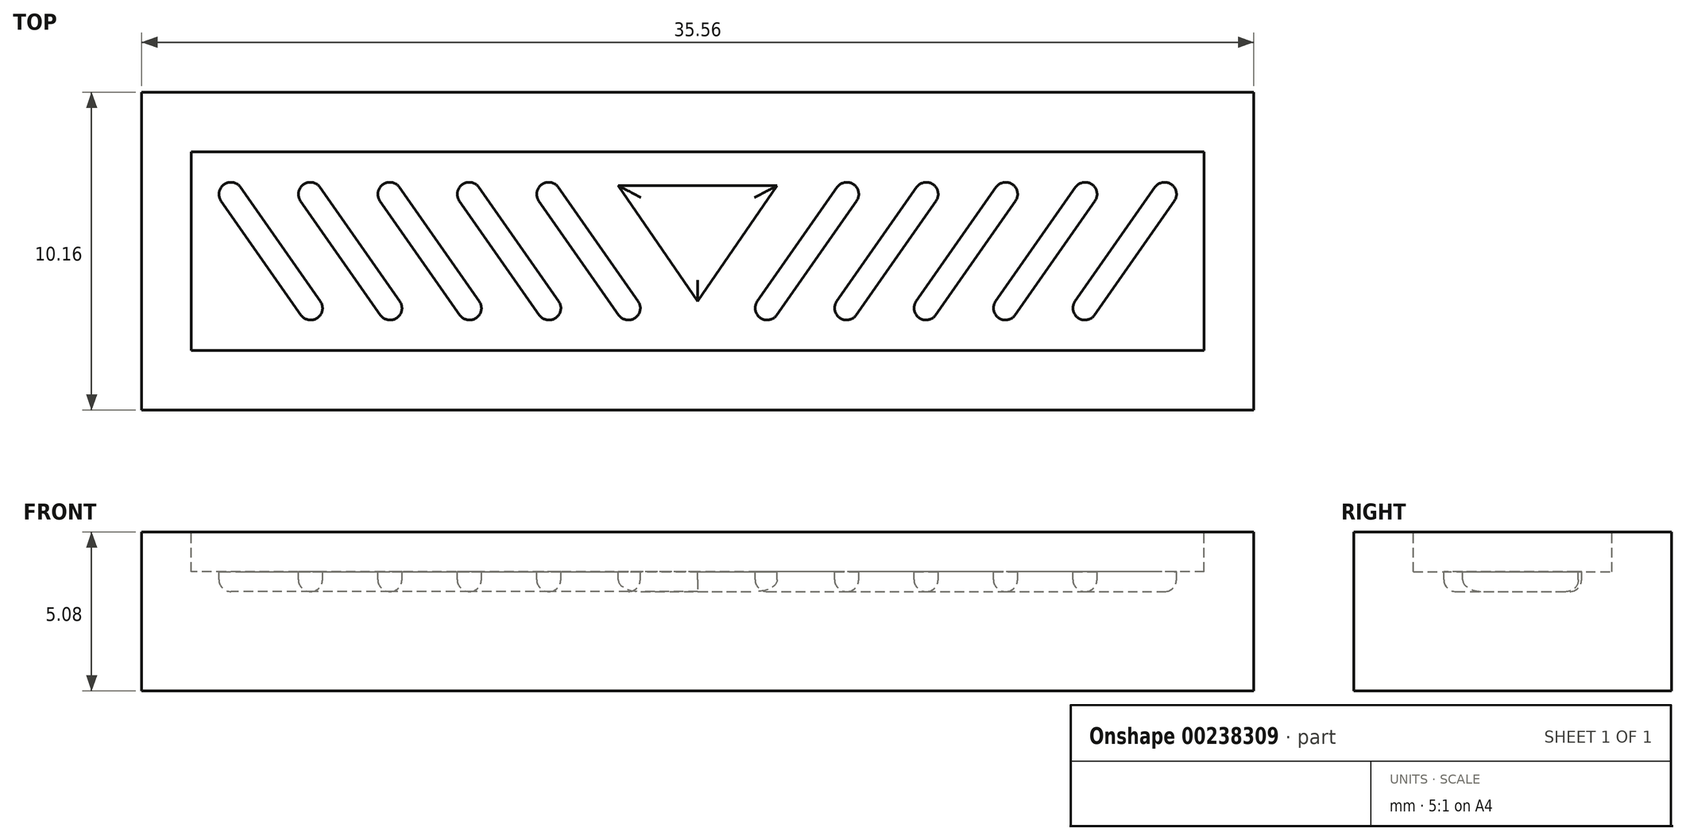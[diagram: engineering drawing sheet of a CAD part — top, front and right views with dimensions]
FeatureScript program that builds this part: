
annotation { "Feature Type Name" : "Feature", "Feature Type Description" : "" }
export const myFeature = defineFeature(function(context is Context, id is Id, definition is map)
    precondition{}
    {
        {
            var Q0;
            Q0=qCreatedBy(makeId("Top.planeOp"),FACE);
            var sketch = newSketch(context, id + "F0", { "sketchPlane" : qUnion([Q0])});
            skLineSegment(sketch, "E0.bottom", {"start": v(17.78, -5.08) * mm, "end": v(-17.78, -5.08) * mm});
            skLineSegment(sketch, "E0.top", {"start": v(17.78, 5.08) * mm, "end": v(-17.78, 5.08) * mm});
            skLineSegment(sketch, "E0.left", {"start": v(17.78, -5.08) * mm, "end": v(17.78, 5.08) * mm});
            skLineSegment(sketch, "E0.right", {"start": v(-17.78, -5.08) * mm, "end": v(-17.78, 5.08) * mm});
            skPoint(sketch, "E0.middle", {"position": v(0, 0) * mm});
            skSolve(sketch);
        }
        {
            var Q0;
            Q0=makeQuery(id+"F0.imprint","IMPRINT",FACE,{"disambiguationData":[TD([[makeQuery(id+"F0.imprint","IMPRINT",EDGE,{"derivedFrom":sQuery(id+"F0.wireOp",EDGE,"E0.bottom")}),-1.0]])]});
            extrude(context, id + "F1", {"entities" : qUnion([Q0]), "depth" : 5.08 * mm});
        }
        {
            var Q0;
            Q0=makeQuery(id+"F1.opExtrude","CAP_FACE",FACE,{"disambiguationData":[OSD([sQuery(id+"F0.wireOp",EDGE,"E0.bottom"),sQuery(id+"F0.wireOp",EDGE,"E0.top"),sQuery(id+"F0.wireOp",EDGE,"E0.left"),sQuery(id+"F0.wireOp",EDGE,"E0.right")])],"isStart":false});
            var sketch = newSketch(context, id + "F2", { "sketchPlane" : qUnion([Q0])});
            skLineSegment(sketch, "E1.bottom", {"start": v(16.2, -3.18) * mm, "end": v(-16.2, -3.18) * mm});
            skLineSegment(sketch, "E1.top", {"start": v(16.2, 3.18) * mm, "end": v(-16.2, 3.18) * mm});
            skLineSegment(sketch, "E1.left", {"start": v(16.2, -3.18) * mm, "end": v(16.2, 3.17) * mm});
            skLineSegment(sketch, "E1.right", {"start": v(-16.2, -3.18) * mm, "end": v(-16.2, 3.17) * mm});
            skPoint(sketch, "E1.middle", {"position": v(0, 0) * mm});
            skSolve(sketch);
        }
        {
            var Q0;
            Q0=qSketchRegion(id+"F2",true);
            extrude(context, id + "F3", {"entities" : qUnion([Q0]), "operationType" : NewBodyOperationType.REMOVE, "oppositeDirection" : true, "depth" : 1.27 * mm});
        }
        {
            var Q0;
            Q0=makeQuery(id+"F3.boolean.opBoolean","COPY",FACE,{"derivedFrom":makeQuery(id+"F3.opExtrude","CAP_FACE",FACE,{"disambiguationData":[OSD([sQuery(id+"F2.wireOp",EDGE,"E1.bottom"),sQuery(id+"F2.wireOp",EDGE,"E1.top"),sQuery(id+"F2.wireOp",EDGE,"E1.left"),sQuery(id+"F2.wireOp",EDGE,"E1.right")])],"isStart":false})});
            var sketch = newSketch(context, id + "F4", { "sketchPlane" : qUnion([Q0])});
            skLineSegment(sketch, "E2", {"start": v(-14.93, 1.82) * mm, "end": v(-12.38, -1.82) * mm});
            skArc(sketch, "E3.0.startCap", {"start": v(-15.24, 1.6) * mm, "mid": v(-15.15, 2.13) * mm, "end": v(-14.62, 2.04) * mm});
            skArc(sketch, "E3.0.endCap", {"start": v(-12.07, -1.6) * mm, "mid": v(-12.16, -2.13) * mm, "end": v(-12.69, -2.04) * mm});
            skLineSegment(sketch, "E3.0.left", {"start": v(-14.62, 2.04) * mm, "end": v(-12.07, -1.6) * mm});
            skLineSegment(sketch, "E3.0.right", {"start": v(-15.24, 1.6) * mm, "end": v(-12.69, -2.04) * mm});
            skPoint(sketch, "E4", {"position": v(-13.65, 0) * mm});
            skLineSegment(sketch, "E5.1.0.0", {"start": v(-12.08, 2.04) * mm, "end": v(-9.53, -1.6) * mm});
            skArc(sketch, "E5.1.0.1", {"start": v(-12.7, 1.6) * mm, "mid": v(-12.6, 2.13) * mm, "end": v(-12.08, 2.04) * mm});
            skLineSegment(sketch, "E5.1.0.2", {"start": v(-12.7, 1.6) * mm, "end": v(-10.15, -2.04) * mm});
            skArc(sketch, "E5.1.0.3", {"start": v(-9.53, -1.6) * mm, "mid": v(-9.62, -2.13) * mm, "end": v(-10.15, -2.04) * mm});
            skLineSegment(sketch, "E5.2.0.0", {"start": v(-9.54, 2.04) * mm, "end": v(-6.99, -1.6) * mm});
            skArc(sketch, "E5.2.0.1", {"start": v(-10.16, 1.6) * mm, "mid": v(-10.07, 2.13) * mm, "end": v(-9.54, 2.04) * mm});
            skLineSegment(sketch, "E5.2.0.2", {"start": v(-10.16, 1.6) * mm, "end": v(-7.6, -2.04) * mm});
            skArc(sketch, "E5.2.0.3", {"start": v(-6.99, -1.6) * mm, "mid": v(-7.08, -2.13) * mm, "end": v(-7.6, -2.04) * mm});
            skLineSegment(sketch, "E5.3.0.0", {"start": v(-7, 2.04) * mm, "end": v(-4.45, -1.6) * mm});
            skArc(sketch, "E5.3.0.1", {"start": v(-7.62, 1.6) * mm, "mid": v(-7.53, 2.13) * mm, "end": v(-7, 2.04) * mm});
            skLineSegment(sketch, "E5.3.0.2", {"start": v(-7.62, 1.6) * mm, "end": v(-5.07, -2.04) * mm});
            skArc(sketch, "E5.3.0.3", {"start": v(-4.45, -1.6) * mm, "mid": v(-4.54, -2.13) * mm, "end": v(-5.07, -2.04) * mm});
            skLineSegment(sketch, "E5.4.0.0", {"start": v(-4.46, 2.04) * mm, "end": v(-1.9, -1.6) * mm});
            skArc(sketch, "E5.4.0.1", {"start": v(-5.08, 1.6) * mm, "mid": v(-4.99, 2.13) * mm, "end": v(-4.46, 2.04) * mm});
            skLineSegment(sketch, "E5.4.0.2", {"start": v(-5.08, 1.6) * mm, "end": v(-2.53, -2.04) * mm});
            skArc(sketch, "E5.4.0.3", {"start": v(-1.9, -1.6) * mm, "mid": v(-2, -2.13) * mm, "end": v(-2.53, -2.04) * mm});
            skLineSegment(sketch, "E5.direction1", {"start": v(-12.69, -2.04) * mm, "end": v(-10.15, -2.04) * mm, "construction": true});
            skLineSegment(sketch, "E6", {"start": v(0, 3.17) * mm, "end": v(0, -3.18) * mm, "construction": true});
            skLineSegment(sketch, "E7.MirrorCS", {"start": v(15.24, 1.6) * mm, "end": v(12.69, -2.04) * mm});
            skLineSegment(sketch, "E8.MirrorCS", {"start": v(14.62, 2.04) * mm, "end": v(12.07, -1.6) * mm});
            skArc(sketch, "E9.MirrorCS", {"start": v(15.24, 1.6) * mm, "mid": v(15.15, 2.13) * mm, "end": v(14.62, 2.04) * mm});
            skArc(sketch, "E10.MirrorCS", {"start": v(12.07, -1.6) * mm, "mid": v(12.16, -2.13) * mm, "end": v(12.69, -2.04) * mm});
            skLineSegment(sketch, "E11.MirrorCS", {"start": v(12.7, 1.6) * mm, "end": v(10.15, -2.04) * mm});
            skArc(sketch, "E12.MirrorCS", {"start": v(12.7, 1.6) * mm, "mid": v(12.6, 2.13) * mm, "end": v(12.08, 2.04) * mm});
            skLineSegment(sketch, "E13.MirrorCS", {"start": v(12.08, 2.04) * mm, "end": v(9.53, -1.6) * mm});
            skArc(sketch, "E14.MirrorCS", {"start": v(9.53, -1.6) * mm, "mid": v(9.62, -2.13) * mm, "end": v(10.15, -2.04) * mm});
            skArc(sketch, "E15.MirrorCS", {"start": v(6.99, -1.6) * mm, "mid": v(7.08, -2.13) * mm, "end": v(7.6, -2.04) * mm});
            skLineSegment(sketch, "E16.MirrorCS", {"start": v(10.16, 1.6) * mm, "end": v(7.6, -2.04) * mm});
            skLineSegment(sketch, "E17.MirrorCS", {"start": v(9.54, 2.04) * mm, "end": v(6.99, -1.6) * mm});
            skArc(sketch, "E18.MirrorCS", {"start": v(10.16, 1.6) * mm, "mid": v(10.07, 2.13) * mm, "end": v(9.54, 2.04) * mm});
            skArc(sketch, "E19.MirrorCS", {"start": v(7.62, 1.6) * mm, "mid": v(7.53, 2.13) * mm, "end": v(7, 2.04) * mm});
            skArc(sketch, "E20.MirrorCS", {"start": v(5.08, 1.6) * mm, "mid": v(4.99, 2.13) * mm, "end": v(4.46, 2.04) * mm});
            skLineSegment(sketch, "E21.MirrorCS", {"start": v(7.62, 1.6) * mm, "end": v(5.07, -2.04) * mm});
            skLineSegment(sketch, "E22.MirrorCS", {"start": v(7, 2.04) * mm, "end": v(4.45, -1.6) * mm});
            skLineSegment(sketch, "E23.MirrorCS", {"start": v(5.08, 1.6) * mm, "end": v(2.53, -2.04) * mm});
            skLineSegment(sketch, "E24.MirrorCS", {"start": v(4.46, 2.04) * mm, "end": v(1.9, -1.6) * mm});
            skArc(sketch, "E25.MirrorCS", {"start": v(4.45, -1.6) * mm, "mid": v(4.54, -2.13) * mm, "end": v(5.07, -2.04) * mm});
            skArc(sketch, "E26.MirrorCS", {"start": v(1.9, -1.6) * mm, "mid": v(2, -2.13) * mm, "end": v(2.53, -2.04) * mm});
            skLineSegment(sketch, "E27", {"start": v(0, -1.6) * mm, "end": v(-2.54, 2.1) * mm});
            skLineSegment(sketch, "E28", {"start": v(-2.54, 2.1) * mm, "end": v(0, 2.1) * mm});
            skLineSegment(sketch, "E29", {"start": v(0, 2.1) * mm, "end": v(0, -1.6) * mm});
            skLineSegment(sketch, "E30.MirrorCS", {"start": v(2.54, 2.1) * mm, "end": v(0, 2.1) * mm});
            skLineSegment(sketch, "E31.MirrorCS", {"start": v(0, -1.6) * mm, "end": v(2.54, 2.1) * mm});
            skSolve(sketch);
        }
        {
            var Q0;
            Q0 = qSketchRegion(id + "F4", true);
            extrude(context, id + "F5", {"entities" : qUnion([Q0]), "operationType" : NewBodyOperationType.REMOVE, "oppositeDirection" : true, "depth" : 0.64 * mm});
        }
        {
            var Q0;
            Q0=makeQuery(id+"F5.boolean.opBoolean","COPY",EDGE,{"derivedFrom":makeQuery(id+"F5.opExtrude","CAP_EDGE",EDGE,{"disambiguationData":[OSD([sQuery(id+"F4.wireOp",EDGE,"E5.1.0.0")])],"isStart":false})});
            var Q1;
            Q1=makeQuery(id+"F5.boolean.opBoolean","COPY",EDGE,{"derivedFrom":makeQuery(id+"F5.opExtrude","CAP_EDGE",EDGE,{"disambiguationData":[OSD([sQuery(id+"F4.wireOp",EDGE,"E3.0.right")])],"isStart":false})});
            var Q2;
            Q2=makeQuery(id+"F5.boolean.opBoolean","COPY",EDGE,{"derivedFrom":makeQuery(id+"F5.opExtrude","CAP_EDGE",EDGE,{"disambiguationData":[OSD([sQuery(id+"F4.wireOp",EDGE,"E5.2.0.2")])],"isStart":false})});
            var Q3;
            Q3=makeQuery(id+"F5.boolean.opBoolean","COPY",EDGE,{"derivedFrom":makeQuery(id+"F5.opExtrude","CAP_EDGE",EDGE,{"disambiguationData":[OSD([sQuery(id+"F4.wireOp",EDGE,"E5.3.0.2")])],"isStart":false})});
            var Q4;
            Q4=makeQuery(id+"F5.boolean.opBoolean","COPY",EDGE,{"derivedFrom":makeQuery(id+"F5.opExtrude","CAP_EDGE",EDGE,{"disambiguationData":[OSD([sQuery(id+"F4.wireOp",EDGE,"E5.4.0.2")])],"isStart":false})});
            var Q5;
            Q5=makeQuery(id+"F5.boolean.opBoolean","COPY",EDGE,{"derivedFrom":makeQuery(id+"F5.opExtrude","CAP_EDGE",EDGE,{"disambiguationData":[OSD([sQuery(id+"F4.wireOp",EDGE,"E24.MirrorCS")])],"isStart":false})});
            var Q6;
            Q6=makeQuery(id+"F5.boolean.opBoolean","COPY",EDGE,{"derivedFrom":makeQuery(id+"F5.opExtrude","CAP_EDGE",EDGE,{"disambiguationData":[OSD([sQuery(id+"F4.wireOp",EDGE,"E22.MirrorCS")])],"isStart":false})});
            var Q7;
            Q7=makeQuery(id+"F5.boolean.opBoolean","COPY",EDGE,{"derivedFrom":makeQuery(id+"F5.opExtrude","CAP_EDGE",EDGE,{"disambiguationData":[OSD([sQuery(id+"F4.wireOp",EDGE,"E17.MirrorCS")])],"isStart":false})});
            var Q8;
            Q8=makeQuery(id+"F5.boolean.opBoolean","COPY",EDGE,{"derivedFrom":makeQuery(id+"F5.opExtrude","CAP_EDGE",EDGE,{"disambiguationData":[OSD([sQuery(id+"F4.wireOp",EDGE,"E13.MirrorCS")])],"isStart":false})});
            var Q9;
            Q9=makeQuery(id+"F5.boolean.opBoolean","COPY",EDGE,{"derivedFrom":makeQuery(id+"F5.opExtrude","CAP_EDGE",EDGE,{"disambiguationData":[OSD([sQuery(id+"F4.wireOp",EDGE,"E8.MirrorCS")])],"isStart":false})});
            var Q10;
            Q10=makeQuery(id+"F5.boolean.opBoolean","COPY",EDGE,{"derivedFrom":makeQuery(id+"F5.opExtrude","CAP_EDGE",EDGE,{"disambiguationData":[OSD([sQuery(id+"F4.wireOp",EDGE,"E28"),sQuery(id+"F4.wireOp",EDGE,"E30.MirrorCS")])],"isStart":false})});
            var Q11;
            Q11=makeQuery(id+"F5.boolean.opBoolean","COPY",EDGE,{"derivedFrom":makeQuery(id+"F5.opExtrude","CAP_EDGE",EDGE,{"disambiguationData":[OSD([sQuery(id+"F4.wireOp",EDGE,"E27")])],"isStart":false})});
            var Q12;
            Q12=makeQuery(id+"F5.boolean.opBoolean","COPY",EDGE,{"derivedFrom":makeQuery(id+"F5.opExtrude","CAP_EDGE",EDGE,{"disambiguationData":[OSD([sQuery(id+"F4.wireOp",EDGE,"E31.MirrorCS")])],"isStart":false})});
            fillet(context, id + "F6", {"entities" : qUnion([Q0, Q1, Q2, Q3, Q4, Q5, Q6, Q7, Q8, Q9, Q10, Q11, Q12]), "radius" : 0.38 * mm, "tangentPropagation" : true, "allowEdgeOverflow" : false});
        }
    });
